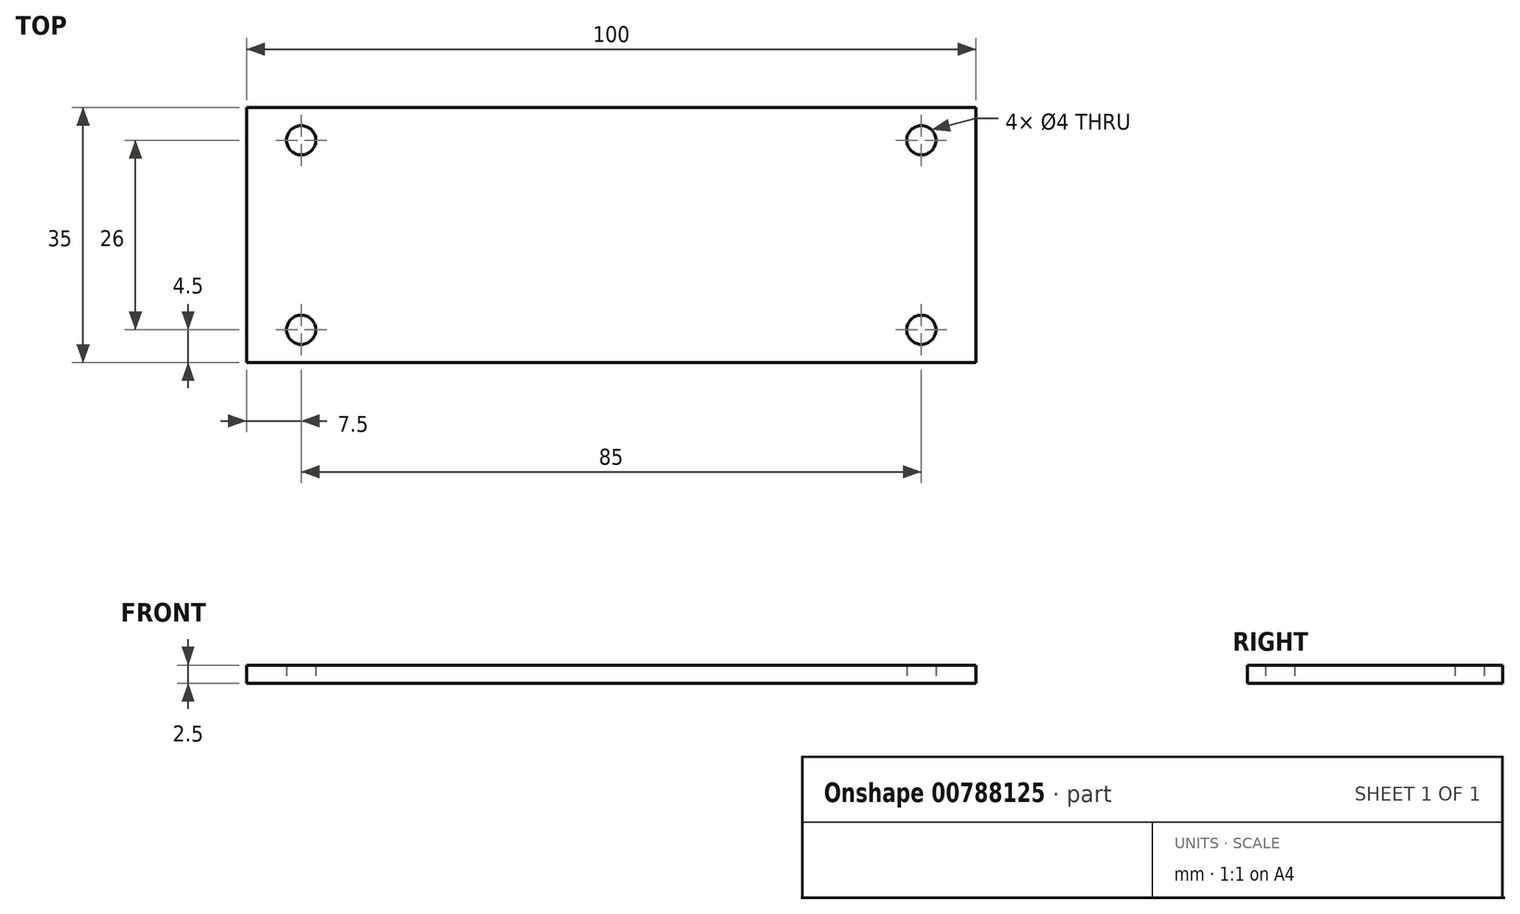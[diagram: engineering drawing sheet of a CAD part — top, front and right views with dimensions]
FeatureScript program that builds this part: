
annotation { "Feature Type Name" : "Feature", "Feature Type Description" : "" }
export const myFeature = defineFeature(function(context is Context, id is Id, definition is map)
    precondition{}
    {
        {
            var Q0;
            Q0=qCreatedBy(makeId("Top.planeOp"),FACE);
            var sketch = newSketch(context, id + "F0", { "sketchPlane" : qUnion([Q0])});
            skLineSegment(sketch, "E0.bottom", {"start": v(0, 0) * mm, "end": v(100, 0) * mm});
            skLineSegment(sketch, "E0.top", {"start": v(0, 35) * mm, "end": v(100, 35) * mm});
            skLineSegment(sketch, "E0.left", {"start": v(0, 0) * mm, "end": v(0, 35) * mm});
            skLineSegment(sketch, "E0.right", {"start": v(100, 0) * mm, "end": v(100, 35) * mm});
            skCircle(sketch, "E1", {"center": v(7.5, 30.5) * mm, "radius": 2 * mm});
            skCircle(sketch, "E2", {"center": v(7.5, 4.5) * mm, "radius": 2 * mm});
            skCircle(sketch, "E3", {"center": v(92.5, 30.5) * mm, "radius": 2 * mm});
            skCircle(sketch, "E4", {"center": v(92.5, 4.5) * mm, "radius": 2 * mm});
            skSolve(sketch);
        }
        {
            var Q0;
            Q0 = qSketchRegion(id + "F0", true);
            extrude(context, id + "F1", {"entities" : qUnion([Q0]), "depth" : 2.5 * mm, "offsetDistance" : 25 * mm});
        }
    });
